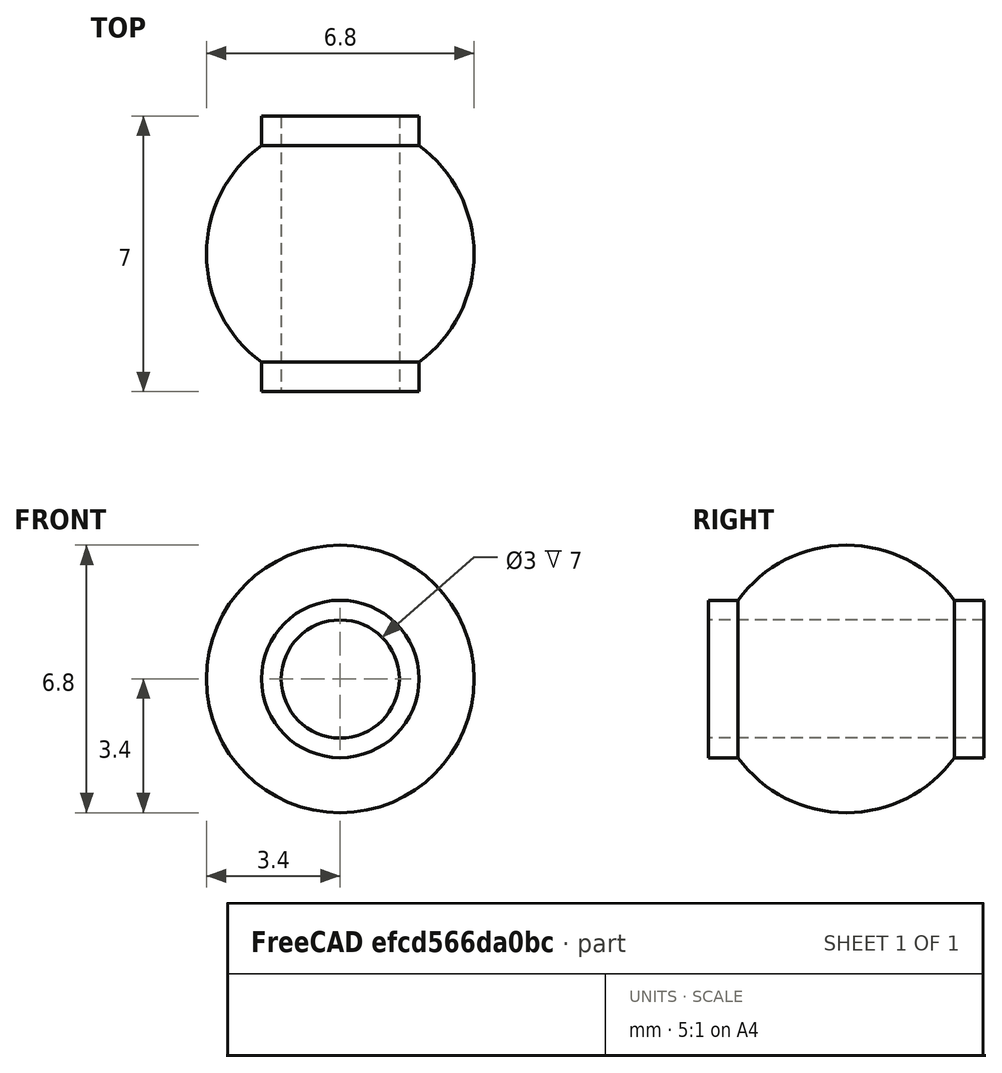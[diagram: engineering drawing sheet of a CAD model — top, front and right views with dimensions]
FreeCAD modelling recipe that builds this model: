
FCSTD DOCUMENT  (FreeCAD 0.16R6706 (Git))
Label: rod_end_ball
License: CreativeCommons Attribution-ShareAlike
LicenseURL: http://creativecommons.org/licenses/by-sa/4.0/
objects: Sketcher::SketchObject×1, PartDesign::Revolution×1
note: 3 computed .brp shape members not serialized (recipe doc carries the construction recipe); baked Part::Feature solids carry a one-line shape summary decoded from their .brp

FEATURE [Sketcher::SketchObject] Sketch
  sketch-geometry (6):
    g0: LineSegment StartX=2 StartY=-3.5 StartZ=0 EndX=2 EndY=-2.74955 EndZ=0
    g1: ArcOfCircle CenterX=0 CenterY=0 CenterZ=0 NormalX=0 NormalY=0 NormalZ=1 Radius=3.4 StartAngle=5.34126 EndAngle=7.22511
    g2: LineSegment StartX=2 StartY=2.74955 StartZ=0 EndX=2 EndY=3.5 EndZ=0
    g3: LineSegment StartX=2 StartY=3.5 StartZ=0 EndX=1.5 EndY=3.5 EndZ=0
    g4: LineSegment StartX=1.5 StartY=3.5 StartZ=0 EndX=1.5 EndY=-3.5 EndZ=0
    g5: LineSegment StartX=1.5 StartY=-3.5 StartZ=0 EndX=2 EndY=-3.5 EndZ=0
  constraints (18):
    c: Coincident(g2,g1)
    c: Vertical(g2)
    c: Coincident(g1,g-1)
    c: Vertical(g0)
    c: Coincident(g1,g0)
    c: DistanceY(g0,g2) = 7
    c: Coincident(g3,g2)
    c: Coincident(g3,g4)
    c: Vertical(g4)
    c: Coincident(g4,g5)
    c: Coincident(g5,g0)
    c: Horizontal(g5)
    c: Horizontal(g3)
    c: DistanceX(g-1,g3) = 1.5
    c: Radius(g1) = 3.4
    c: PointOnObject(g1,g0)
    c: Equal(g2,g0)
    c: DistanceX(g5,g5) = 0.5
FEATURE [PartDesign::Revolution] Revolution
  Angle = 360
  Axis = (0,1,0)
  Base = (0,0,0)
  ReferenceAxis = -> Sketch [V_Axis]
  Reversed = true
  Sketch = -> Sketch
